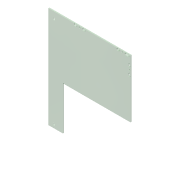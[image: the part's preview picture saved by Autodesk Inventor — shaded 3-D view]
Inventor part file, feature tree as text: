
AUTODESK INVENTOR PART (.ipt)
format: ipt  version: 2017 (Build 210142000, 142)  size: 472,576 bytes
history: native  units: mm
features: sketch x7, extrude x5, hole x2, projected_geometry x1
ambient origin geometry x8: Origin, YZ Plane, XZ Plane, XY Plane, X Axis, Y Axis, Z Axis, Center Point
bodies: Solid1 (feature_tree)
feature tree (15):
  extrude  "Extrusion1"  Depth=3.0mm TaperAngle=0.0deg
  hole  "Hole1"  [1 undecoded]
  hole  "Hole2"  [1 undecoded]
  extrude  "Extrusion2"  [1 undecoded]
  extrude  "Extrusion3"  [1 undecoded]
  extrude  "Extrusion4"  [1 undecoded]
  extrude  "Extrusion5"  [1 undecoded]
  sketch  "Sketch1"  dims[d0=3.0mm d1=0.0mm]
  sketch  "Sketch2"  dims[d2=3.2mm d3=6.0mm d4=4.0mm d5=2.0mm d6=90.0deg d7=8.0mm d8=20.594885mm]
  projected_geometry  "Projected Loop1"
  sketch  "Sketch5"  dims[d9=5.2mm d10=6.0mm d11=4.0mm d12=2.0mm d13=90.0deg d14=8.0mm d15=20.594885mm d16=3.0mm d17=0.0mm]
  sketch  "Sketch6"  dims[d18=5.2mm d19=3.0mm d20=0.0mm]
  sketch  "Sketch7"  dims[d21=3.0mm d22=0.0mm d23=0.0mm d24=0.0mm]
  sketch  "Sketch8"
  sketch  "Sketch9"
note: 6 required parameter values undecoded (feature->parameter linkage not recoverable at this tier; creation-order binding heuristic only, values carry confidence <= 0.55)
